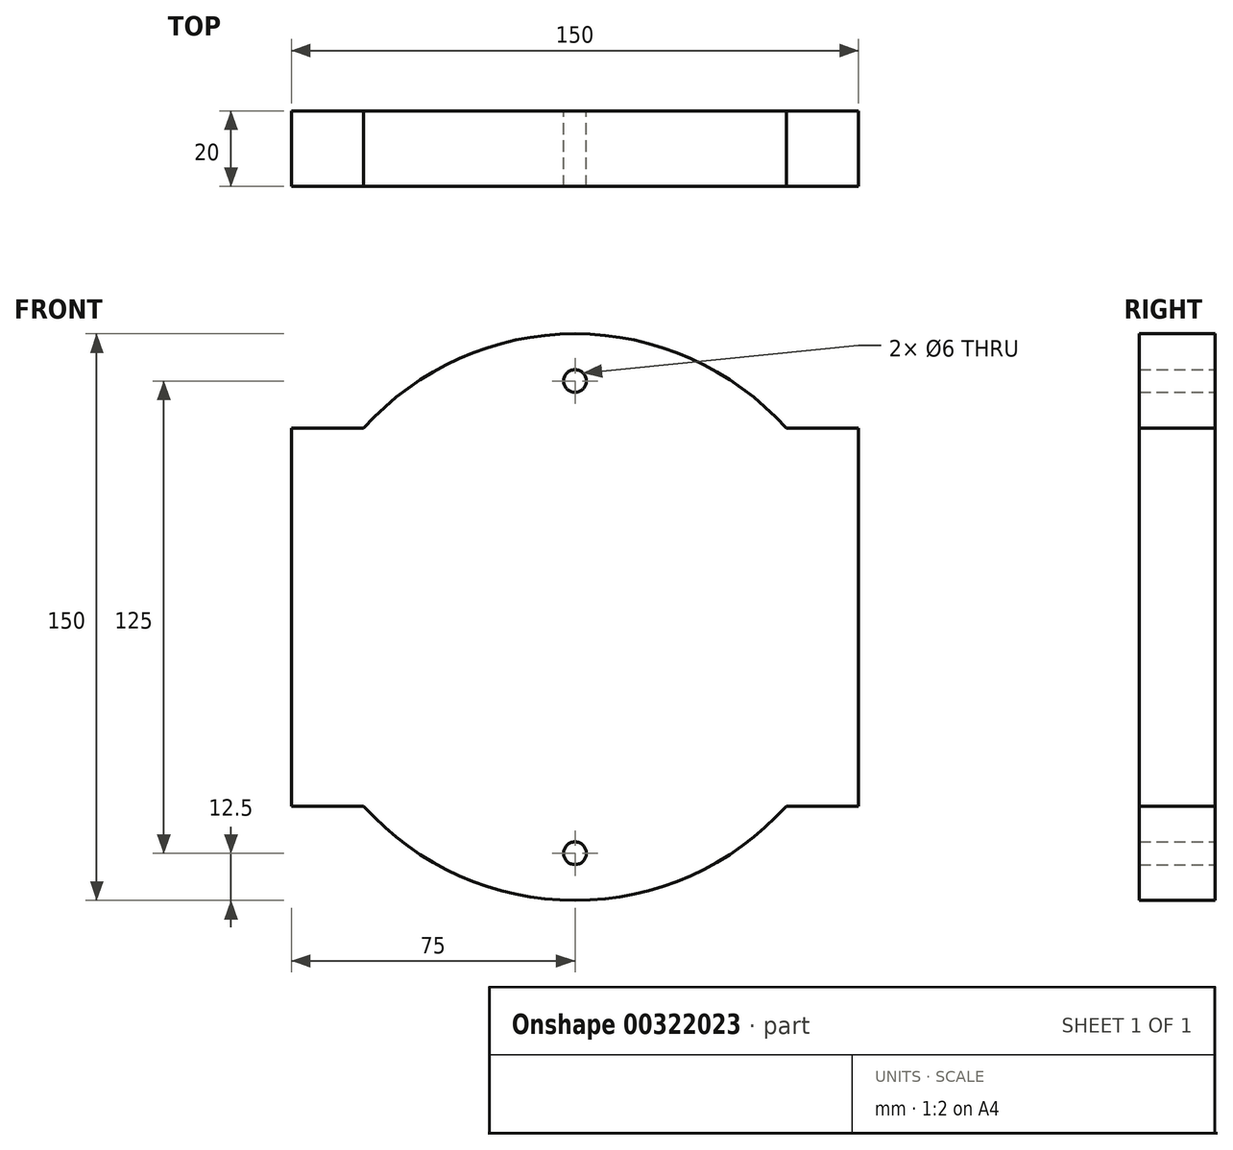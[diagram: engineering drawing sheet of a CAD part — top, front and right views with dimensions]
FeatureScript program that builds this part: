
annotation { "Feature Type Name" : "Feature", "Feature Type Description" : "" }
export const myFeature = defineFeature(function(context is Context, id is Id, definition is map)
    precondition{}
    {
        {
            var Q0;
            Q0=qCreatedBy(makeId("Front.planeOp"),FACE);
            var sketch = newSketch(context, id + "F0", { "sketchPlane" : qUnion([Q0])});
            skLineSegment(sketch, "E0.bottom", {"start": v(-75, 50) * mm, "end": v(-55.9, 50) * mm});
            skLineSegment(sketch, "E0.top", {"start": v(-75, -50) * mm, "end": v(-55.9, -50) * mm});
            skLineSegment(sketch, "E0.left", {"start": v(-75, 50) * mm, "end": v(-75, -50) * mm});
            skLineSegment(sketch, "E0.right", {"start": v(75, 50) * mm, "end": v(75, -50) * mm});
            skPoint(sketch, "E0.middle", {"position": v(0, 0) * mm});
            skArc(sketch, "E1", {"start": v(-55.9, -50) * mm, "mid": v(0, -75) * mm, "end": v(55.9, -50) * mm});
            skArc(sketch, "E2.trimOffspring", {"start": v(55.9, 50) * mm, "mid": v(0, 75) * mm, "end": v(-55.9, 50) * mm});
            skLineSegment(sketch, "E3.trimOffspring", {"start": v(55.9, 50) * mm, "end": v(75, 50) * mm});
            skLineSegment(sketch, "E4.trimOffspring", {"start": v(55.9, -50) * mm, "end": v(75, -50) * mm});
            skCircle(sketch, "E5", {"center": v(0, 62.5) * mm, "radius": 3 * mm});
            skCircle(sketch, "E6", {"center": v(0, -62.5) * mm, "radius": 3 * mm});
            skSolve(sketch);
        }
        {
            var Q0;
            Q0=makeQuery(id+"F0.imprint","IMPRINT",FACE,{"disambiguationData":[TD([[makeQuery(id+"F0.imprint","IMPRINT",EDGE,{"derivedFrom":sQuery(id+"F0.wireOp",EDGE,"E0.bottom")}),-1.0]])]});
            extrude(context, id + "F1", {"entities" : qUnion([Q0]), "depth" : 20 * mm});
        }
    });
